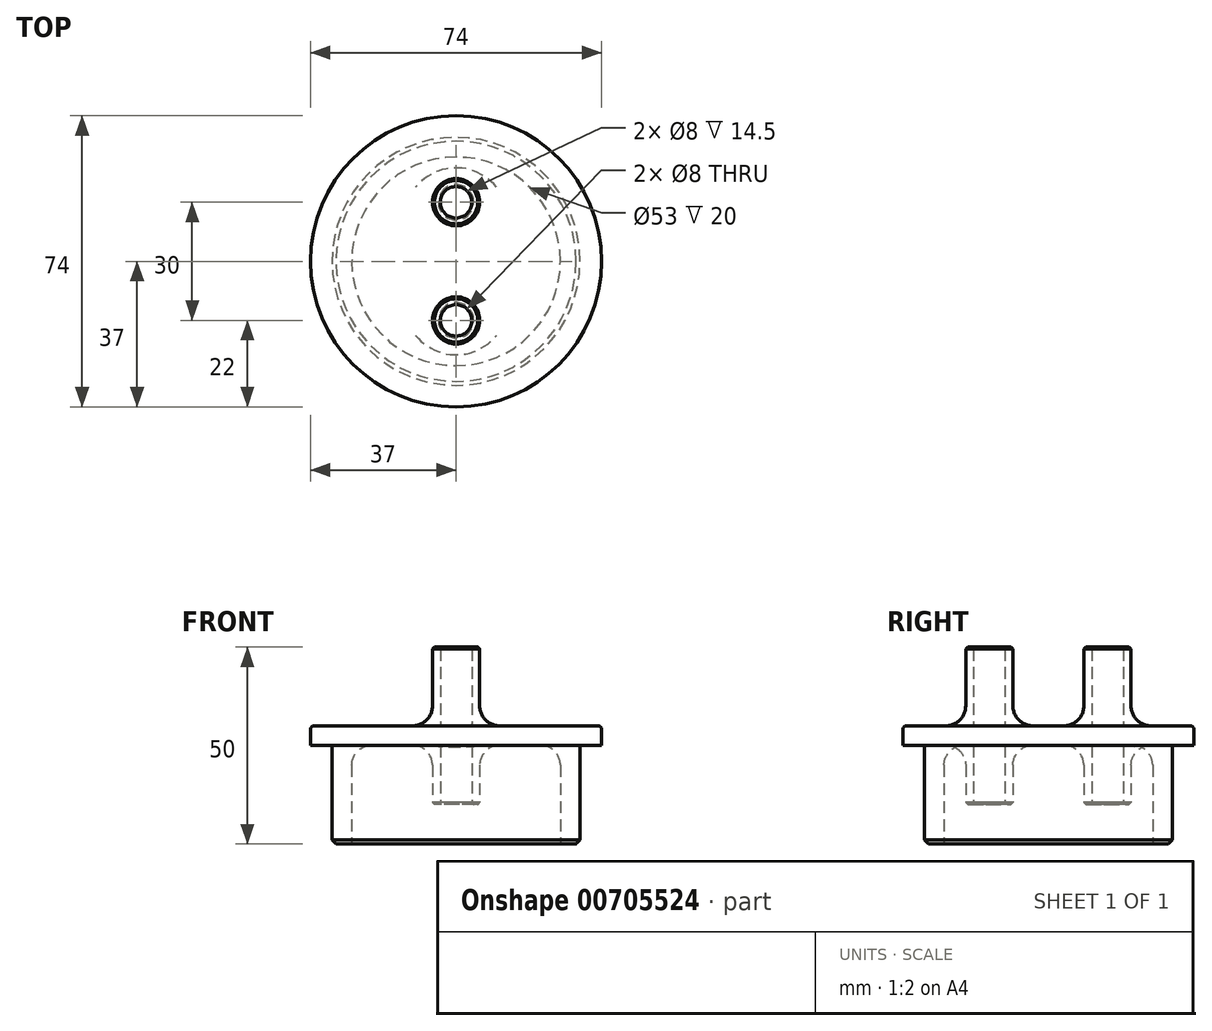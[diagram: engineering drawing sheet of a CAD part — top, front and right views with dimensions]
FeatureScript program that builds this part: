
annotation { "Feature Type Name" : "Feature", "Feature Type Description" : "" }
export const myFeature = defineFeature(function(context is Context, id is Id, definition is map)
    precondition{}
    {
        {
            var Q0;
            Q0=qCreatedBy(makeId("Top.planeOp"),FACE);
            var sketch = newSketch(context, id + "F0", { "sketchPlane" : qUnion([Q0])});
            skCircle(sketch, "E0", {"center": v(0, 0) * mm, "radius": 31.5 * mm});
            skCircle(sketch, "E1", {"center": v(0, 0) * mm, "radius": 26.5 * mm});
            skSolve(sketch);
        }
        {
            var Q0;
            Q0=makeQuery(id+"F0.imprint","IMPRINT",FACE,{"disambiguationData":[TD([[makeQuery(id+"F0.imprint","IMPRINT",EDGE,{"derivedFrom":sQuery(id+"F0.wireOp",EDGE,"E0")}),1.0]])]});
            extrude(context, id + "F1", {"entities" : qUnion([Q0]), "depth" : 25 * mm, "offsetDistance" : 25 * mm});
        }
        {
            var Q0;
            Q0=makeQuery(id+"F1.opExtrude","CAP_FACE",FACE,{"disambiguationData":[OSD([sQuery(id+"F0.wireOp",EDGE,"E0"),sQuery(id+"F0.wireOp",EDGE,"E1")])],"isStart":false});
            var sketch = newSketch(context, id + "F2", { "sketchPlane" : qUnion([Q0])});
            skCircle(sketch, "E2", {"center": v(0, 0) * mm, "radius": 37 * mm});
            skSolve(sketch);
        }
        {
            var Q0;
            Q0=makeQuery(id+"F2.imprint","IMPRINT",FACE,{"disambiguationData":[TD([[makeQuery(id+"F2.imprint","IMPRINT",EDGE,{"derivedFrom":makeQuery(id+"F1.opExtrude","CAP_EDGE",EDGE,{"disambiguationData":[OSD([sQuery(id+"F0.wireOp",EDGE,"E1")])],"isStart":false})}),1.0]])]});
            var Q1;
            Q1=makeQuery(id+"F2.imprint","IMPRINT",FACE,{"disambiguationData":[TD([[makeQuery(id+"F2.imprint","IMPRINT",EDGE,{"derivedFrom":makeQuery(id+"F1.opExtrude","CAP_EDGE",EDGE,{"disambiguationData":[OSD([sQuery(id+"F0.wireOp",EDGE,"E0")])],"isStart":false})}),1.0]])]});
            var Q2;
            Q2=makeQuery(id+"F2.imprint","IMPRINT",FACE,{"disambiguationData":[TD([[makeQuery(id+"F2.imprint","IMPRINT",EDGE,{"derivedFrom":sQuery(id+"F2.wireOp",EDGE,"E2")}),1.0]])]});
            extrude(context, id + "F3", {"entities" : qUnion([Q0, Q1, Q2]), "operationType" : NewBodyOperationType.ADD, "depth" : 5 * mm, "offsetDistance" : 25 * mm});
        }
        {
            var Q0;
            Q0=makeQuery(id+"F3.opExtrude","CAP_FACE",FACE,{"disambiguationData":[OSD([sQuery(id+"F2.wireOp",EDGE,"E2")])],"isStart":false});
            var sketch = newSketch(context, id + "F4", { "sketchPlane" : qUnion([Q0])});
            skCircle(sketch, "E3", {"center": v(0, 15) * mm, "radius": 6 * mm});
            skCircle(sketch, "E4.1.0", {"center": v(0, -15) * mm, "radius": 6 * mm});
            skPoint(sketch, "E4.center", {"position": v(0, 0) * mm});
            skCircle(sketch, "E5.0", {"center": v(0, 15) * mm, "radius": 4 * mm});
            skCircle(sketch, "E6.0", {"center": v(0, -15) * mm, "radius": 4 * mm});
            skSolve(sketch);
        }
        {
            var Q0;
            Q0=makeQuery(id+"F4.imprint","IMPRINT",FACE,{"disambiguationData":[TD([[makeQuery(id+"F4.imprint","IMPRINT",EDGE,{"derivedFrom":sQuery(id+"F4.wireOp",EDGE,"E4.1.0")}),1.0]])]});
            var Q1;
            Q1=makeQuery(id+"F4.imprint","IMPRINT",FACE,{"disambiguationData":[TD([[makeQuery(id+"F4.imprint","IMPRINT",EDGE,{"derivedFrom":sQuery(id+"F4.wireOp",EDGE,"E3")}),1.0]])]});
            extrude(context, id + "F5", {"entities" : qUnion([Q0, Q1]), "operationType" : NewBodyOperationType.ADD, "endBound" : BoundingType.SYMMETRIC, "depth" : 40 * mm, "offsetDistance" : 25 * mm});
        }
        {
            var Q0;
            Q0=makeQuery(id+"F5.boolean.opBoolean","INTERSECT",EDGE,{"derivedFrom":[makeQuery(id+"F3.opExtrude","CAP_FACE",FACE,{"disambiguationData":[OSD([sQuery(id+"F2.wireOp",EDGE,"E2")])],"isStart":false}),makeQuery(id+"F5.opExtrude","SWEPT_FACE",FACE,{"disambiguationData":[OSD([sQuery(id+"F4.wireOp",EDGE,"E3")])]})]});
            var Q1;
            Q1=makeQuery(id+"F5.boolean.opBoolean","INTERSECT",EDGE,{"derivedFrom":[makeQuery(id+"F3.opExtrude","CAP_FACE",FACE,{"disambiguationData":[OSD([sQuery(id+"F2.wireOp",EDGE,"E2")])],"isStart":false}),makeQuery(id+"F5.opExtrude","SWEPT_FACE",FACE,{"disambiguationData":[OSD([sQuery(id+"F4.wireOp",EDGE,"E4.1.0")])]})]});
            var Q2;
            {var subQ0=makeQuery(id+"F1.opExtrude","SWEPT_FACE",FACE,{"disambiguationData":[OSD([sQuery(id+"F0.wireOp",EDGE,"E1")])]});Q2=makeQuery(id+"F5.boolean.opBoolean","SPLIT",FACE,{"disambiguationData":[TD([subQ0])],"derivedFrom":makeQuery(id+"F3.boolean.opBoolean","SPLIT",FACE,{"disambiguationData":[TD([subQ0])],"derivedFrom":makeQuery(id+"F3.opExtrude","CAP_FACE",FACE,{"disambiguationData":[OSD([sQuery(id+"F2.wireOp",EDGE,"E2")])],"isStart":true})})});}
            fillet(context, id + "F6", {"entities" : qUnion([Q0, Q1, Q2]), "radius" : 5 * mm, "tangentPropagation" : true, "allowEdgeOverflow" : false});
        }
        {
            var Q0;
            Q0=makeQuery(id+"F3.opExtrude","CAP_EDGE",EDGE,{"disambiguationData":[OSD([sQuery(id+"F2.wireOp",EDGE,"E2")])],"isStart":false});
            fillet(context, id + "F7", {"entities" : qUnion([Q0]), "radius" : 1 * mm, "tangentPropagation" : true, "allowEdgeOverflow" : false});
        }
        {
            var Q0;
            Q0=makeQuery(id+"F1.opExtrude","CAP_EDGE",EDGE,{"disambiguationData":[OSD([sQuery(id+"F0.wireOp",EDGE,"E0")])],"isStart":true});
            chamfer(context, id + "F8", {"entities" : qUnion([Q0]), "width" : 1 * mm, "tangentPropagation" : true});
        }
        {
            var Q0;
            {var subQ0=sQuery(id+"F4.wireOp",EDGE,"E5.0");Q0=makeQuery(id+"F5.boolean.opBoolean","SPLIT",FACE,{"disambiguationData":[TD([makeQuery(id+"F3.opExtrude","CAP_FACE",FACE,{"disambiguationData":[OSD([sQuery(id+"F2.wireOp",EDGE,"E2")])],"isStart":false})])],"derivedFrom":makeQuery(id+"F5.opExtrude","SWEPT_FACE",FACE,{"disambiguationData":[OSD([subQ0])]})});}
            var Q1;
            {var subQ0=sQuery(id+"F4.wireOp",EDGE,"E6.0");Q1=makeQuery(id+"F5.boolean.opBoolean","SPLIT",FACE,{"disambiguationData":[TD([makeQuery(id+"F3.opExtrude","CAP_FACE",FACE,{"disambiguationData":[OSD([sQuery(id+"F2.wireOp",EDGE,"E2")])],"isStart":false})])],"derivedFrom":makeQuery(id+"F5.opExtrude","SWEPT_FACE",FACE,{"disambiguationData":[OSD([subQ0])]})});}
            fillet(context, id + "F9", {"entities" : qUnion([Q0, Q1]), "radius" : .5 * mm, "tangentPropagation" : true, "allowEdgeOverflow" : false});
        }
        {
            var Q0;
            Q0=makeQuery(id+"F5.opExtrude","CAP_EDGE",EDGE,{"disambiguationData":[OSD([sQuery(id+"F4.wireOp",EDGE,"E4.1.0")])],"isStart":false});
            var Q1;
            Q1=makeQuery(id+"F5.opExtrude","CAP_EDGE",EDGE,{"disambiguationData":[OSD([sQuery(id+"F4.wireOp",EDGE,"E3")])],"isStart":false});
            chamfer(context, id + "F10", {"entities" : qUnion([Q0, Q1]), "width" : .5 * mm, "tangentPropagation" : true});
        }
        {
            var Q0;
            Q0=makeQuery(id+"F5.opExtrude","CAP_EDGE",EDGE,{"disambiguationData":[OSD([sQuery(id+"F4.wireOp",EDGE,"E5.0")])],"isStart":true});
            var Q1;
            Q1=makeQuery(id+"F5.opExtrude","CAP_EDGE",EDGE,{"disambiguationData":[OSD([sQuery(id+"F4.wireOp",EDGE,"E6.0")])],"isStart":true});
            chamfer(context, id + "F11", {"entities" : qUnion([Q0, Q1]), "width" : .5 * mm, "tangentPropagation" : true});
        }
        {
            var Q0;
            Q0=makeQuery(id+"F5.opExtrude","CAP_EDGE",EDGE,{"disambiguationData":[OSD([sQuery(id+"F4.wireOp",EDGE,"E3")])],"isStart":true});
            var Q1;
            Q1=makeQuery(id+"F5.opExtrude","CAP_EDGE",EDGE,{"disambiguationData":[OSD([sQuery(id+"F4.wireOp",EDGE,"E4.1.0")])],"isStart":true});
            chamfer(context, id + "F12", {"entities" : qUnion([Q0, Q1]), "width" : .5 * mm, "tangentPropagation" : true});
        }
    });
